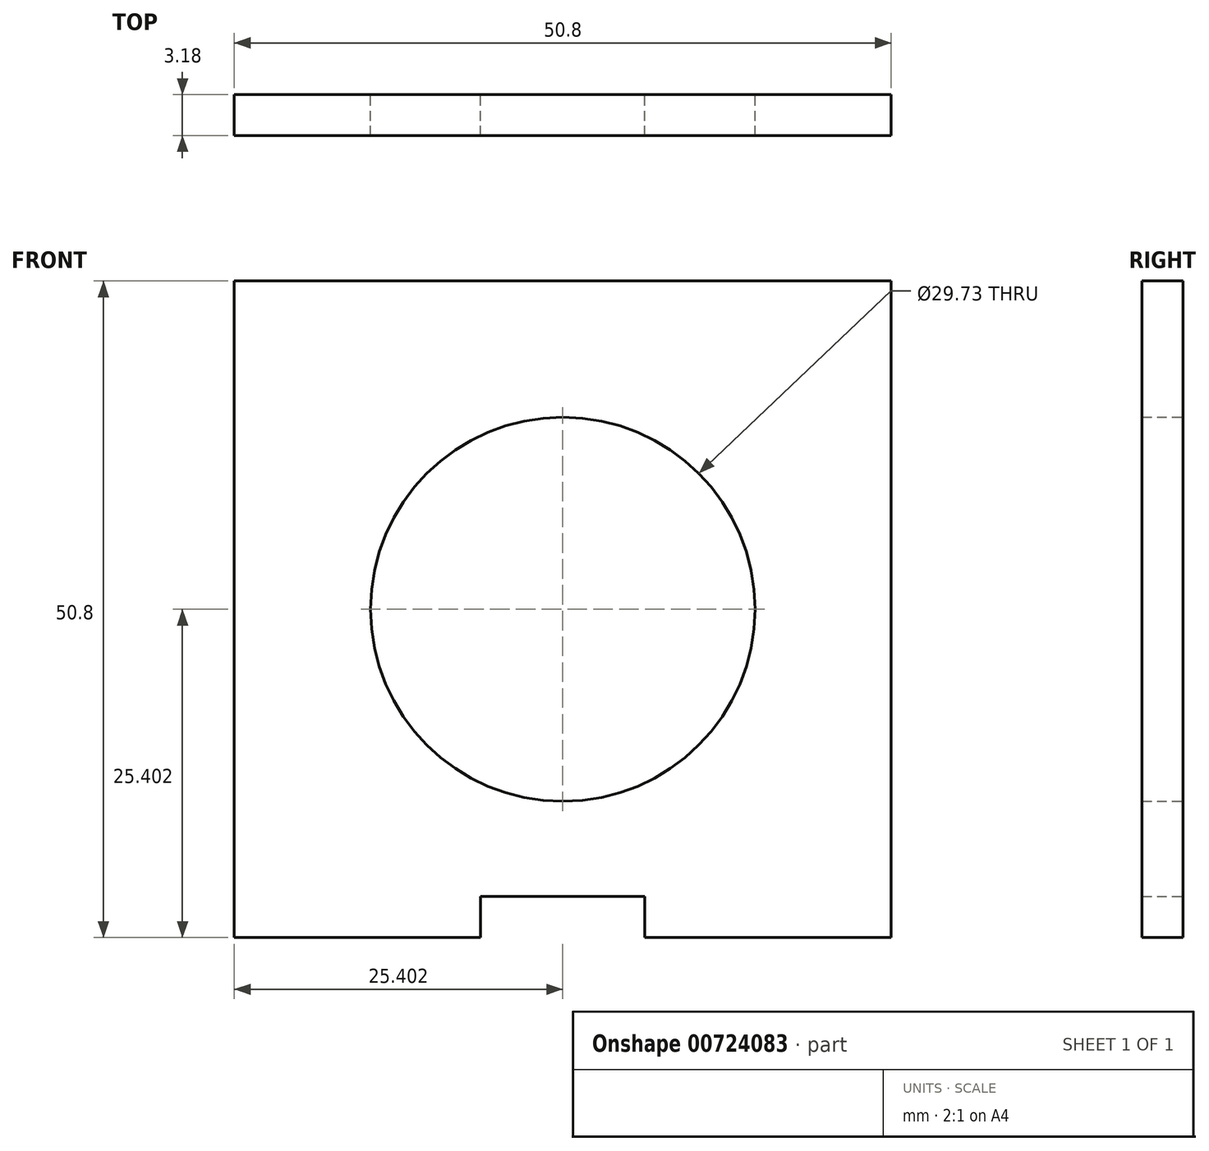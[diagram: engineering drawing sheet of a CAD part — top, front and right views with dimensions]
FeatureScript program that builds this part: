
annotation { "Feature Type Name" : "Feature", "Feature Type Description" : "" }
export const myFeature = defineFeature(function(context is Context, id is Id, definition is map)
    precondition{}
    {
        {
            var Q0;
            Q0=qCreatedBy(makeId("Front.planeOp"),FACE);
            var sketch = newSketch(context, id + "F0", { "sketchPlane" : qUnion([Q0])});
            skLineSegment(sketch, "E0.bottom", {"start": v(-34.85, 34.27) * mm, "end": v(15.95, 34.27) * mm});
            skLineSegment(sketch, "E0.top", {"start": v(-34.85, -16.53) * mm, "end": v(-15.8, -16.53) * mm});
            skLineSegment(sketch, "E0.left", {"start": v(-34.85, 34.27) * mm, "end": v(-34.85, -16.53) * mm});
            skLineSegment(sketch, "E0.right", {"start": v(15.95, 34.27) * mm, "end": v(15.95, -16.53) * mm});
            skLineSegment(sketch, "E1.bottom", {"start": v(-15.8, -13.35) * mm, "end": v(-3.1, -13.35) * mm});
            skLineSegment(sketch, "E1.left", {"start": v(-15.8, -13.35) * mm, "end": v(-15.8, -16.53) * mm});
            skLineSegment(sketch, "E1.right", {"start": v(-3.1, -13.35) * mm, "end": v(-3.1, -16.53) * mm});
            skLineSegment(sketch, "E2.trimOffspring", {"start": v(-3.1, -16.53) * mm, "end": v(15.95, -16.53) * mm});
            skCircle(sketch, "E3", {"center": v(-9.45, 8.87) * mm, "radius": 14.86 * mm});
            skPoint(sketch, "E4.top.end.orphan", {"position": v(-9.45, 34.27) * mm});
            skPoint(sketch, "E5.end.orphan", {"position": v(-34.85, 8.87) * mm});
            skSolve(sketch);
        }
        {
            var Q0;
            Q0 = qSketchRegion(id + "F0", true);
            var Q1;
            Q1=makeQuery(id+"F0.imprint","IMPRINT",FACE,{"disambiguationData":[TD([[makeQuery(id+"F0.imprint","IMPRINT",EDGE,{"derivedFrom":sQuery(id+"F0.wireOp",EDGE,"E0.bottom")}),-1.0]])]});
            extrude(context, id + "F1", {"entities" : qUnion([Q0, Q1]), "depth" : 3.17 * mm, "offsetDistance" : 25.4 * mm});
        }
    });
